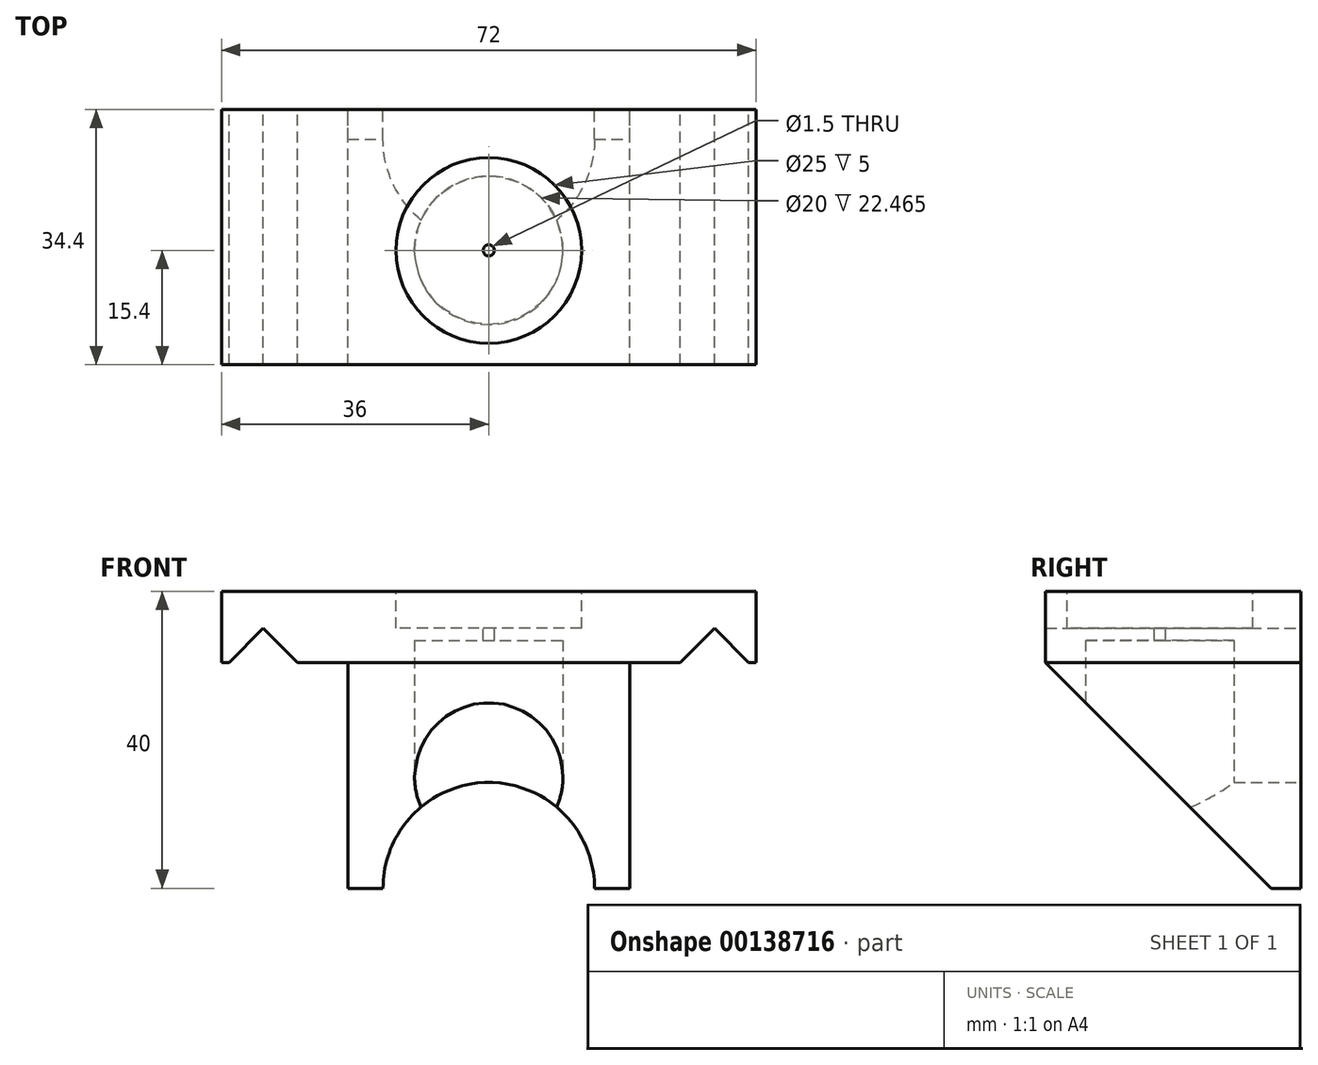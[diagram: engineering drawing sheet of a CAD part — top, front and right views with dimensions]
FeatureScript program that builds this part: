
annotation { "Feature Type Name" : "Feature", "Feature Type Description" : "" }
export const myFeature = defineFeature(function(context is Context, id is Id, definition is map)
    precondition{}
    {
        {
            var Q0;
            Q0=qCreatedBy(makeId("Front.planeOp"),FACE);
            var sketch = newSketch(context, id + "F0", { "sketchPlane" : qUnion([Q0])});
            skLineSegment(sketch, "E0", {"start": v(0, 40) * mm, "end": v(36, 40) * mm});
            skLineSegment(sketch, "E1", {"start": v(36, 40) * mm, "end": v(36, 30.4) * mm});
            skLineSegment(sketch, "E2", {"start": v(36, 30.4) * mm, "end": v(35, 30.4) * mm});
            skLineSegment(sketch, "E3", {"start": v(35, 30.4) * mm, "end": v(30.4, 35) * mm});
            skLineSegment(sketch, "E4", {"start": v(30.4, 35) * mm, "end": v(25.8, 30.4) * mm});
            skLineSegment(sketch, "E5", {"start": v(25.8, 30.4) * mm, "end": v(19, 30.4) * mm});
            skLineSegment(sketch, "E6", {"start": v(19, 30.4) * mm, "end": v(19, 0) * mm});
            skLineSegment(sketch, "E7", {"start": v(19, 0) * mm, "end": v(14.25, 0) * mm});
            skLineSegment(sketch, "E8.MirrorCS", {"start": v(-36, 30.4) * mm, "end": v(-35, 30.4) * mm});
            skLineSegment(sketch, "E9.MirrorCS", {"start": v(-30.4, 35) * mm, "end": v(-25.8, 30.4) * mm});
            skLineSegment(sketch, "E10.MirrorCS", {"start": v(-35, 30.4) * mm, "end": v(-30.4, 35) * mm});
            skLineSegment(sketch, "E11.MirrorCS", {"start": v(0, 40) * mm, "end": v(-36, 40) * mm});
            skLineSegment(sketch, "E12.MirrorCS", {"start": v(-36, 40) * mm, "end": v(-36, 30.4) * mm});
            skLineSegment(sketch, "E13.MirrorCS", {"start": v(-19, 0) * mm, "end": v(-14.25, 0) * mm});
            skLineSegment(sketch, "E14.MirrorCS", {"start": v(-25.8, 30.4) * mm, "end": v(-19, 30.4) * mm});
            skLineSegment(sketch, "E15.MirrorCS", {"start": v(-19, 30.4) * mm, "end": v(-19, 0) * mm});
            skArc(sketch, "E16", {"start": v(14.25, 0) * mm, "mid": v(0, 14.25) * mm, "end": v(-14.25, 0) * mm});
            skSolve(sketch);
        }
        {
            var Q0;
            Q0 = qSketchRegion(id + "F0", true);
            extrude(context, id + "F1", {"entities" : qUnion([Q0]), "depth" : 34.4 * mm});
        }
        {
            var Q0;
            Q0=makeQuery(id+"F1.opExtrude","SWEPT_FACE",FACE,{"disambiguationData":[OSD([sQuery(id+"F0.wireOp",EDGE,"E1")])]});
            var sketch = newSketch(context, id + "F2", { "sketchPlane" : qUnion([Q0])});
            skLineSegment(sketch, "E17", {"start": v(-34.4, 30.4) * mm, "end": v(-4, 0) * mm});
            skLineSegment(sketch, "E18", {"start": v(-4, 0) * mm, "end": v(-34.4, 0) * mm});
            skLineSegment(sketch, "E19", {"start": v(-34.4, 0) * mm, "end": v(-34.4, 30.4) * mm});
            skSolve(sketch);
        }
        {
            var Q0;
            Q0 = qSketchRegion(id + "F2", true);
            extrude(context, id + "F3", {"entities" : qUnion([Q0]), "operationType" : NewBodyOperationType.REMOVE, "endBound" : BoundingType.THROUGH_ALL, "oppositeDirection" : true, "depth" : 25 * mm});
        }
        {
            var Q0;
            Q0=makeQuery(id+"F1.opExtrude","SWEPT_FACE",FACE,{"disambiguationData":[OSD([sQuery(id+"F0.wireOp",EDGE,"E0"),sQuery(id+"F0.wireOp",EDGE,"E11.MirrorCS")])]});
            var sketch = newSketch(context, id + "F4", { "sketchPlane" : qUnion([Q0])});
            skCircle(sketch, "E20", {"center": v(0, -19) * mm, "radius": 0.75 * mm});
            skSolve(sketch);
        }
        {
            var Q0;
            Q0 = qSketchRegion(id + "F4", true);
            extrude(context, id + "F5", {"entities" : qUnion([Q0]), "operationType" : NewBodyOperationType.REMOVE, "endBound" : BoundingType.THROUGH_ALL, "oppositeDirection" : true, "depth" : 25 * mm});
        }
        {
            var Q0;
            Q0=makeQuery(id+"F1.opExtrude","SWEPT_FACE",FACE,{"disambiguationData":[OSD([sQuery(id+"F0.wireOp",EDGE,"E0"),sQuery(id+"F0.wireOp",EDGE,"E11.MirrorCS")])]});
            var sketch = newSketch(context, id + "F6", { "sketchPlane" : qUnion([Q0])});
            skCircle(sketch, "E21", {"center": v(0, -19) * mm, "radius": 12.5 * mm});
            skSolve(sketch);
        }
        {
            var Q0;
            Q0 = qSketchRegion(id + "F6", true);
            extrude(context, id + "F7", {"entities" : qUnion([Q0]), "operationType" : NewBodyOperationType.REMOVE, "oppositeDirection" : true, "depth" : 5 * mm});
        }
        {
            var Q0;
            Q0=makeQuery(id+"F1.opExtrude","SWEPT_FACE",FACE,{"disambiguationData":[OSD([sQuery(id+"F0.wireOp",EDGE,"E7")])]});
            var sketch = newSketch(context, id + "F8", { "sketchPlane" : qUnion([Q0])});
            skCircle(sketch, "E22", {"center": v(0, 19) * mm, "radius": 10 * mm});
            skSolve(sketch);
        }
        {
            var Q0;
            Q0 = qSketchRegion(id + "F8", true);
            extrude(context, id + "F9", {"entities" : qUnion([Q0]), "operationType" : NewBodyOperationType.REMOVE, "oppositeDirection" : true, "depth" : 33.4 * mm});
        }
    });
